# Revit family: Covrit Gate
name_source: partatom
category: Doors
revit_build: Autodesk Revit 2017 (Build: 20190508_0315(x64)
units: mm (PartAtom-declared; Revit-internal decimal feet)

## family parameters
Always vertical = Yes
Cut with Voids When Loaded = No
OmniClass Number = 23.30.10.00
OmniClass Title = Doors
Room Calculation Point = No
Shared = No

## types (3) — shared parameters
Analytic Construction = <None>
Assembly Code = G2040100
Function = Exterior
Gate Rail Width = 0' - 2"
Ground Offset = 0' - 4"
Manufacturer = CityScapes, Inc.
Model = CovRit Gate
Total Gate Rail Height per Panel = 0' - 4"
Version = 191001

## per-type parameters (varying)
| type | Description | Gate Rail Thickness | Not Steel | PVC Panel | PVC Plank | Panel Thickness | Steel Panel | Thickness | Type Comments | URL |
| CityScapes Gate - PVC Panel |  | 0' - 2" | Yes | Yes | No | 0' - 0 1/2" | No | 0' - 0 1/2" |  |  |
| CityScapes Gate - PVC Plank | covRit - Screening systems | 0' - 2" | Yes | No | Yes | 0' - 1" | No | 0' - 1" | Gate System | www.cityscapesinc.com |
| CityScapes Gate - Steel Panel |  | 0' - 3" | No | No | No | 0' - 2" | Yes | 0' - 2" |  | https://cityscapesinc.com |

## geometry (parser evidence)
native form markers: Sweep x7
no freeform markers — native parametric forms only
